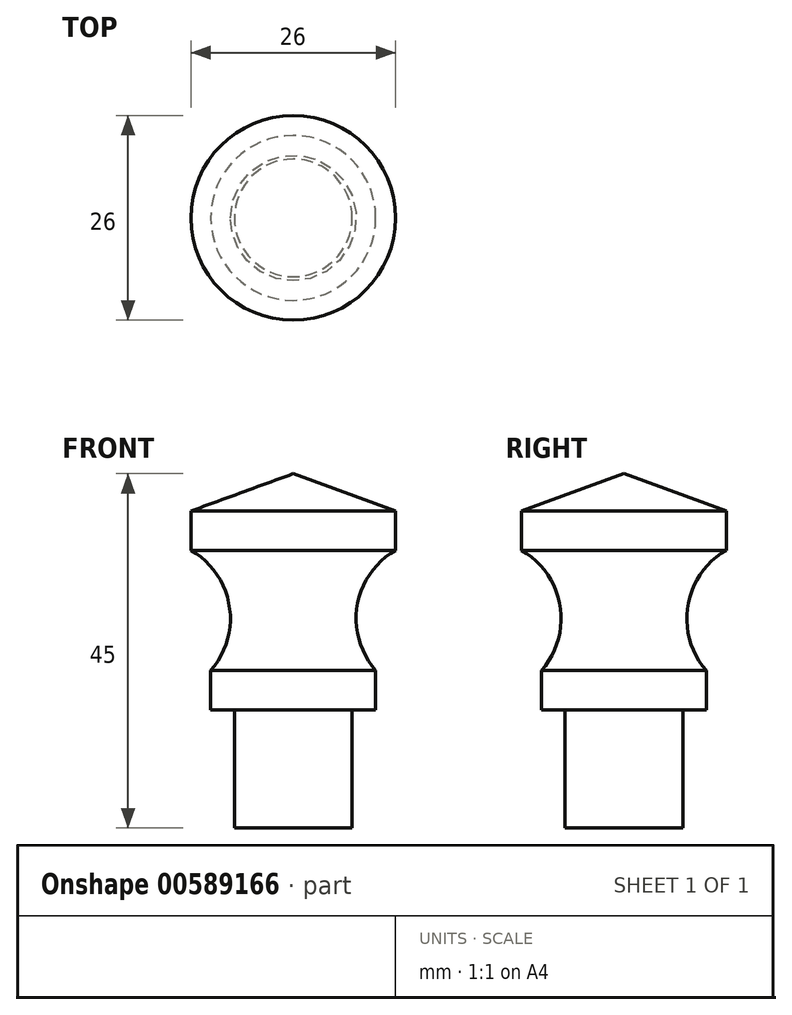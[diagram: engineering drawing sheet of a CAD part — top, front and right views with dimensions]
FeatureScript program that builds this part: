
annotation { "Feature Type Name" : "Feature", "Feature Type Description" : "" }
export const myFeature = defineFeature(function(context is Context, id is Id, definition is map)
    precondition{}
    {
        {
            var Q0;
            Q0=qCreatedBy(makeId("Front.planeOp"),FACE);
            var sketch = newSketch(context, id + "F0", { "sketchPlane" : qUnion([Q0])});
            skLineSegment(sketch, "E0", {"start": v(0, 0) * mm, "end": v(0, 30) * mm});
            skLineSegment(sketch, "E1", {"start": v(0, 30) * mm, "end": v(-13, 25.27) * mm});
            skLineSegment(sketch, "E2", {"start": v(-10.48, 5) * mm, "end": v(-10.48, 0) * mm});
            skLineSegment(sketch, "E3", {"start": v(-10.48, 0) * mm, "end": v(-7.48, 0) * mm});
            skLineSegment(sketch, "E4", {"start": v(-7.48, 0) * mm, "end": v(-7.48, -15) * mm});
            skLineSegment(sketch, "E5", {"start": v(-7.48, -15) * mm, "end": v(0, -15) * mm});
            skLineSegment(sketch, "E6", {"start": v(0, -15) * mm, "end": v(0, 0) * mm});
            skLineSegment(sketch, "E7", {"start": v(-13, 25.27) * mm, "end": v(-13, 20.27) * mm});
            skArc(sketch, "E8", {"start": v(-10.48, 5) * mm, "mid": v(-8.12, 13.23) * mm, "end": v(-13, 20.27) * mm});
            skSolve(sketch);
        }
        {
            var Q0;
            Q0 = qSketchRegion(id + "F0", true);
            var Q1;
            Q1=sQuery(id+"F0.wireOp",EDGE,"E0");
            revolve(context, id + "F1", {"entities" : qUnion([Q0]), "axis" : qUnion([Q1]), "revolveType" : RevolveType.FULL});
        }
    });
